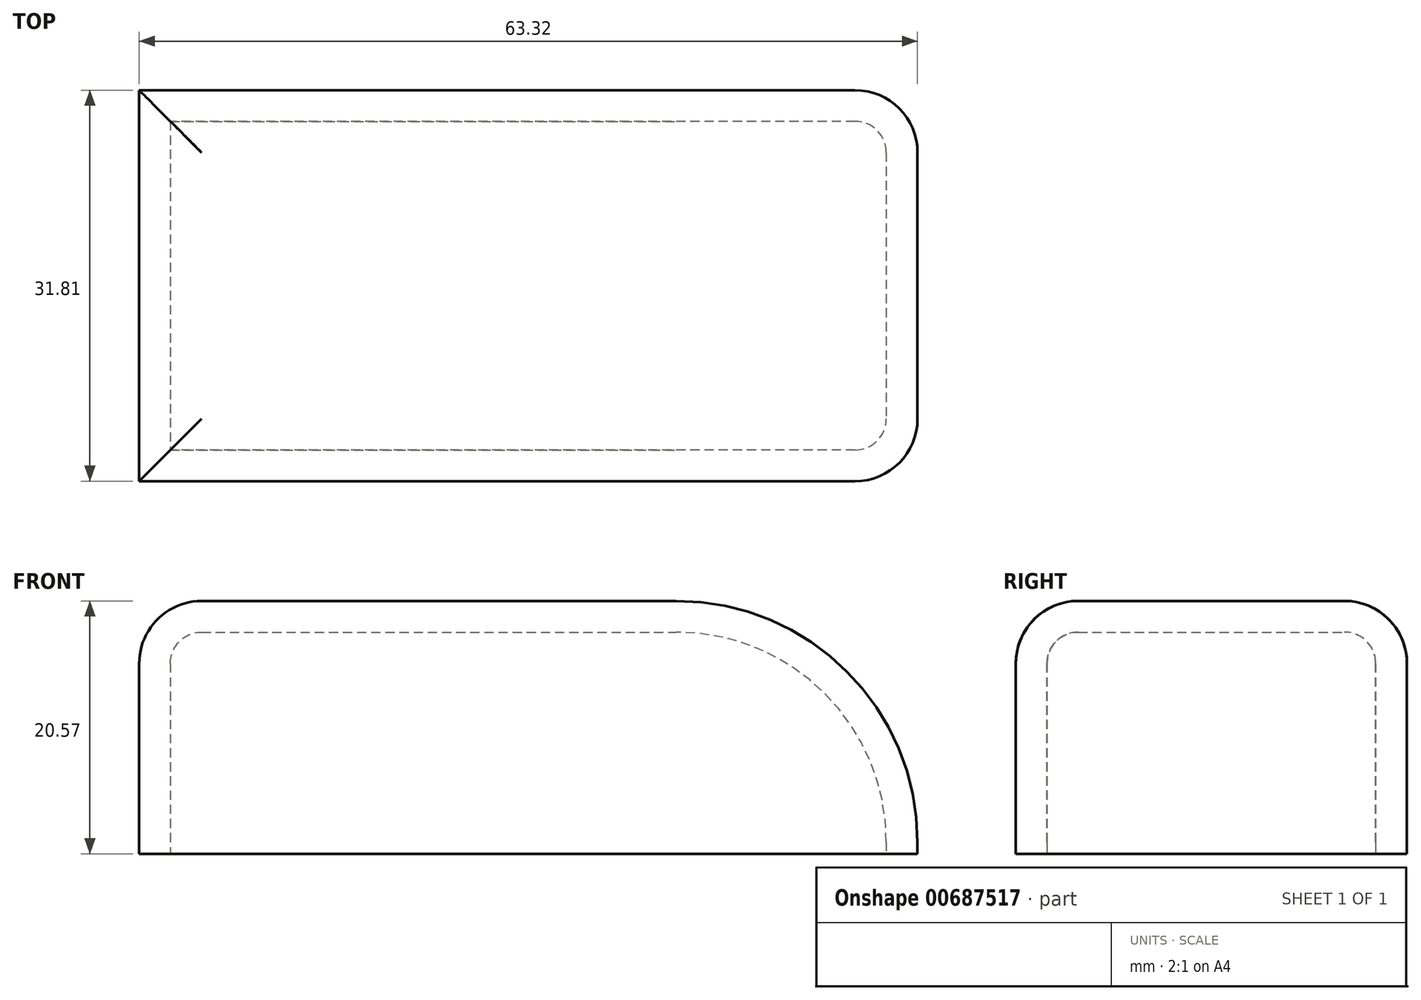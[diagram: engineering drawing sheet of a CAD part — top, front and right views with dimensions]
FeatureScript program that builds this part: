
annotation { "Feature Type Name" : "Feature", "Feature Type Description" : "" }
export const myFeature = defineFeature(function(context is Context, id is Id, definition is map)
    precondition{}
    {
        {
            var Q0;
            Q0=qCreatedBy(makeId("Top.planeOp"),FACE);
            var sketch = newSketch(context, id + "F0", { "sketchPlane" : qUnion([Q0])});
            skLineSegment(sketch, "E0.bottom", {"start": v(0, 0) * mm, "end": v(-63.32, 0) * mm});
            skLineSegment(sketch, "E0.top", {"start": v(0, -31.81) * mm, "end": v(-63.32, -31.81) * mm});
            skLineSegment(sketch, "E0.left", {"start": v(0, 0) * mm, "end": v(0, -31.81) * mm});
            skLineSegment(sketch, "E0.right", {"start": v(-63.32, 0) * mm, "end": v(-63.32, -31.81) * mm});
            skSolve(sketch);
        }
        {
            var Q0;
            Q0 = qSketchRegion(id + "F0", true);
            extrude(context, id + "F1", {"entities" : qUnion([Q0]), "depth" : 20.57 * mm, "offsetDistance" : 25.4 * mm});
        }
        {
            var Q0;
            Q0=makeQuery(id+"F1.opExtrude","CAP_EDGE",EDGE,{"disambiguationData":[OSD([sQuery(id+"F0.wireOp",EDGE,"E0.left")])],"isStart":false});
            fillet(context, id + "F2", {"entities" : qUnion([Q0]), "radius" : 19.62 * mm, "tangentPropagation" : true, "allowEdgeOverflow" : false});
        }
        {
            var Q0;
            Q0=makeQuery(id+"F1.opExtrude","CAP_EDGE",EDGE,{"disambiguationData":[OSD([sQuery(id+"F0.wireOp",EDGE,"E0.top")])],"isStart":false});
            var Q1;
            Q1=makeQuery(id+"F1.opExtrude","CAP_EDGE",EDGE,{"disambiguationData":[OSD([sQuery(id+"F0.wireOp",EDGE,"E0.bottom")])],"isStart":false});
            var Q2;
            Q2=makeQuery(id+"F1.opExtrude","CAP_EDGE",EDGE,{"disambiguationData":[OSD([sQuery(id+"F0.wireOp",EDGE,"E0.right")])],"isStart":false});
            fillet(context, id + "F3", {"entities" : qUnion([Q0, Q1, Q2]), "radius" : 5.08 * mm, "tangentPropagation" : true, "allowEdgeOverflow" : false});
        }
        {
            var Q0;
            Q0=makeQuery(id+"F1.opExtrude","CAP_FACE",FACE,{"disambiguationData":[OSD([sQuery(id+"F0.wireOp",EDGE,"E0.bottom"),sQuery(id+"F0.wireOp",EDGE,"E0.top"),sQuery(id+"F0.wireOp",EDGE,"E0.left"),sQuery(id+"F0.wireOp",EDGE,"E0.right")])],"isStart":true});
            shell(context, id + "F4", {"entities" : qUnion([Q0]), "thickness" : 2.54 * mm});
        }
    });
